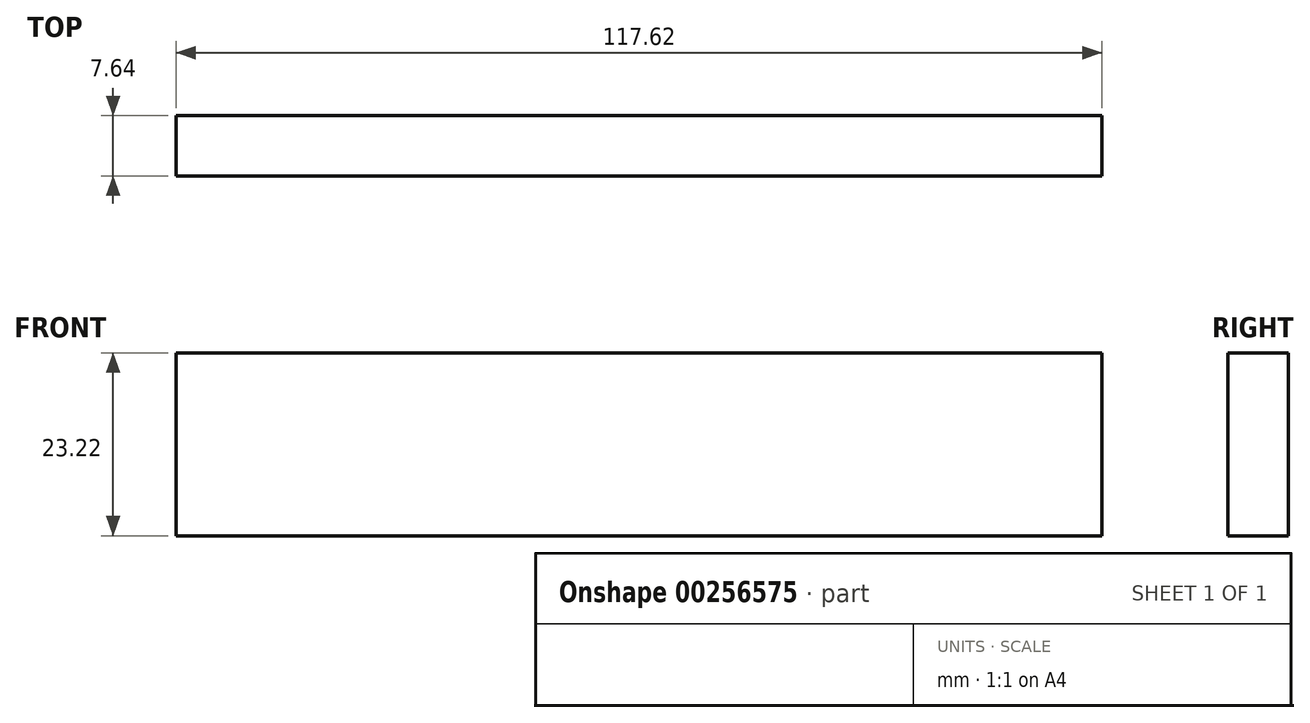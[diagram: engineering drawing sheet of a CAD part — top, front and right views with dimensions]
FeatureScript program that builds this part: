
annotation { "Feature Type Name" : "Feature", "Feature Type Description" : "" }
export const myFeature = defineFeature(function(context is Context, id is Id, definition is map)
    precondition{}
    {
        {
            var Q0;
            Q0=qCreatedBy(makeId("Front.planeOp"),FACE);
            var sketch = newSketch(context, id + "F0", { "sketchPlane" : qUnion([Q0])});
            skLineSegment(sketch, "E0.bottom", {"start": v(-58.81, 11.6) * mm, "end": v(58.81, 11.6) * mm});
            skLineSegment(sketch, "E0.top", {"start": v(-58.81, -11.6) * mm, "end": v(58.81, -11.6) * mm});
            skLineSegment(sketch, "E0.left", {"start": v(-58.81, 11.6) * mm, "end": v(-58.81, -11.6) * mm});
            skLineSegment(sketch, "E0.right", {"start": v(58.81, 11.6) * mm, "end": v(58.81, -11.6) * mm});
            skPoint(sketch, "E0.middle", {"position": v(0, 0) * mm});
            skSolve(sketch);
        }
        {
            var Q0;
            Q0 = qSketchRegion(id + "F0", true);
            extrude(context, id + "F1", {"entities" : qUnion([Q0]), "endBound" : BoundingType.SYMMETRIC, "depth" : 7.65 * mm});
        }
    });
